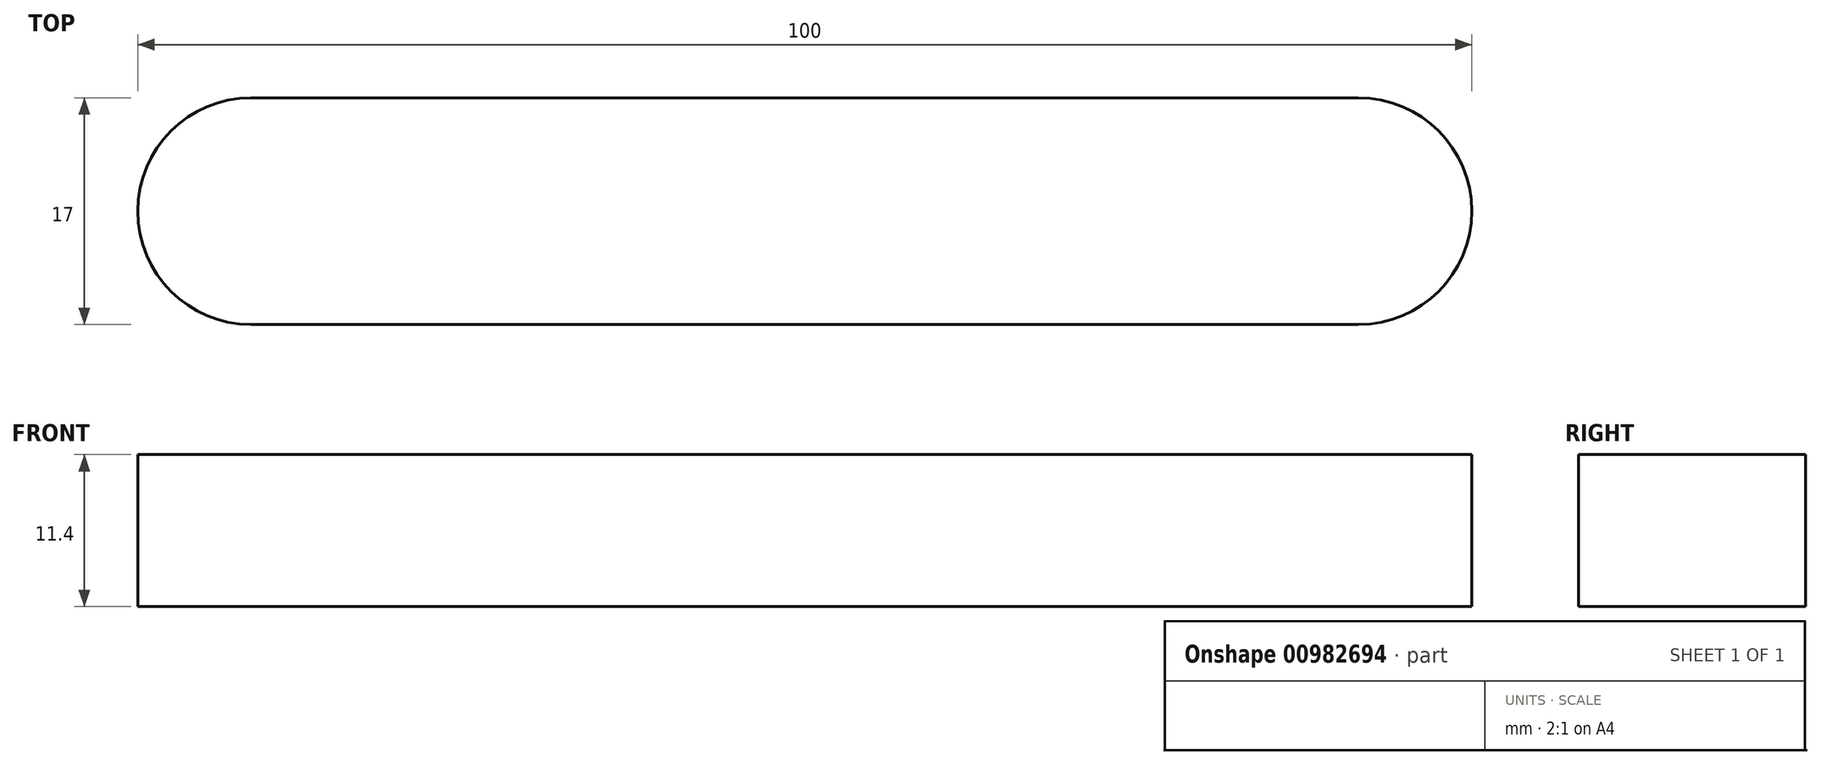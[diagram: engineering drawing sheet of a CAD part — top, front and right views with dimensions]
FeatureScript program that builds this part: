
annotation { "Feature Type Name" : "Feature", "Feature Type Description" : "" }
export const myFeature = defineFeature(function(context is Context, id is Id, definition is map)
    precondition{}
    {
        {
            var Q0;
            Q0=qCreatedBy(makeId("Top.planeOp"),FACE);
            var sketch = newSketch(context, id + "F0", { "sketchPlane" : qUnion([Q0])});
            skCircle(sketch, "E0", {"center": v(0, 0) * mm, "radius": 8.5 * mm});
            skCircle(sketch, "E1", {"center": v(83, 0) * mm, "radius": 8.5 * mm});
            skLineSegment(sketch, "E2", {"start": v(0, 8.5) * mm, "end": v(83, 8.5) * mm});
            skLineSegment(sketch, "E3", {"start": v(83, -8.5) * mm, "end": v(0, -8.5) * mm});
            skSolve(sketch);
        }
        {
            var Q0;
            {var subQ0=sQuery(id+"F0.wireOp",EDGE,"E2");Q0=makeQuery(id+"F0.imprint","IMPRINT",FACE,{"disambiguationData":[TD([[makeQuery(id+"F0.imprint","IMPRINT",EDGE,{"derivedFrom":subQ0}),-1.0]])]});}
            var Q1;
            {var subQ0=sQuery(id+"F0.wireOp",EDGE,"E0");var subQ1=makeQuery(id+"F0.imprint","INTERSECT",VERTEX,{"derivedFrom":[subQ0,sQuery(id+"F0.wireOp",EDGE,"E2")]});Q1=makeQuery(id+"F0.imprint","IMPRINT",FACE,{"disambiguationData":[TD([[makeQuery(id+"F0.imprint","IMPRINT",EDGE,{"disambiguationData":[TD([[subQ1,-1.0]])],"derivedFrom":subQ0}),1.0]])]});}
            var Q2;
            {var subQ0=sQuery(id+"F0.wireOp",EDGE,"E1");var subQ1=makeQuery(id+"F0.imprint","INTERSECT",VERTEX,{"derivedFrom":[subQ0,sQuery(id+"F0.wireOp",EDGE,"E2")]});Q2=makeQuery(id+"F0.imprint","IMPRINT",FACE,{"disambiguationData":[TD([[makeQuery(id+"F0.imprint","IMPRINT",EDGE,{"disambiguationData":[TD([[subQ1,-1.0]])],"derivedFrom":subQ0}),1.0]])]});}
            extrude(context, id + "F1", {"entities" : qUnion([Q0, Q1, Q2]), "depth" : 11.4 * mm, "offsetDistance" : 25 * mm});
        }
    });
